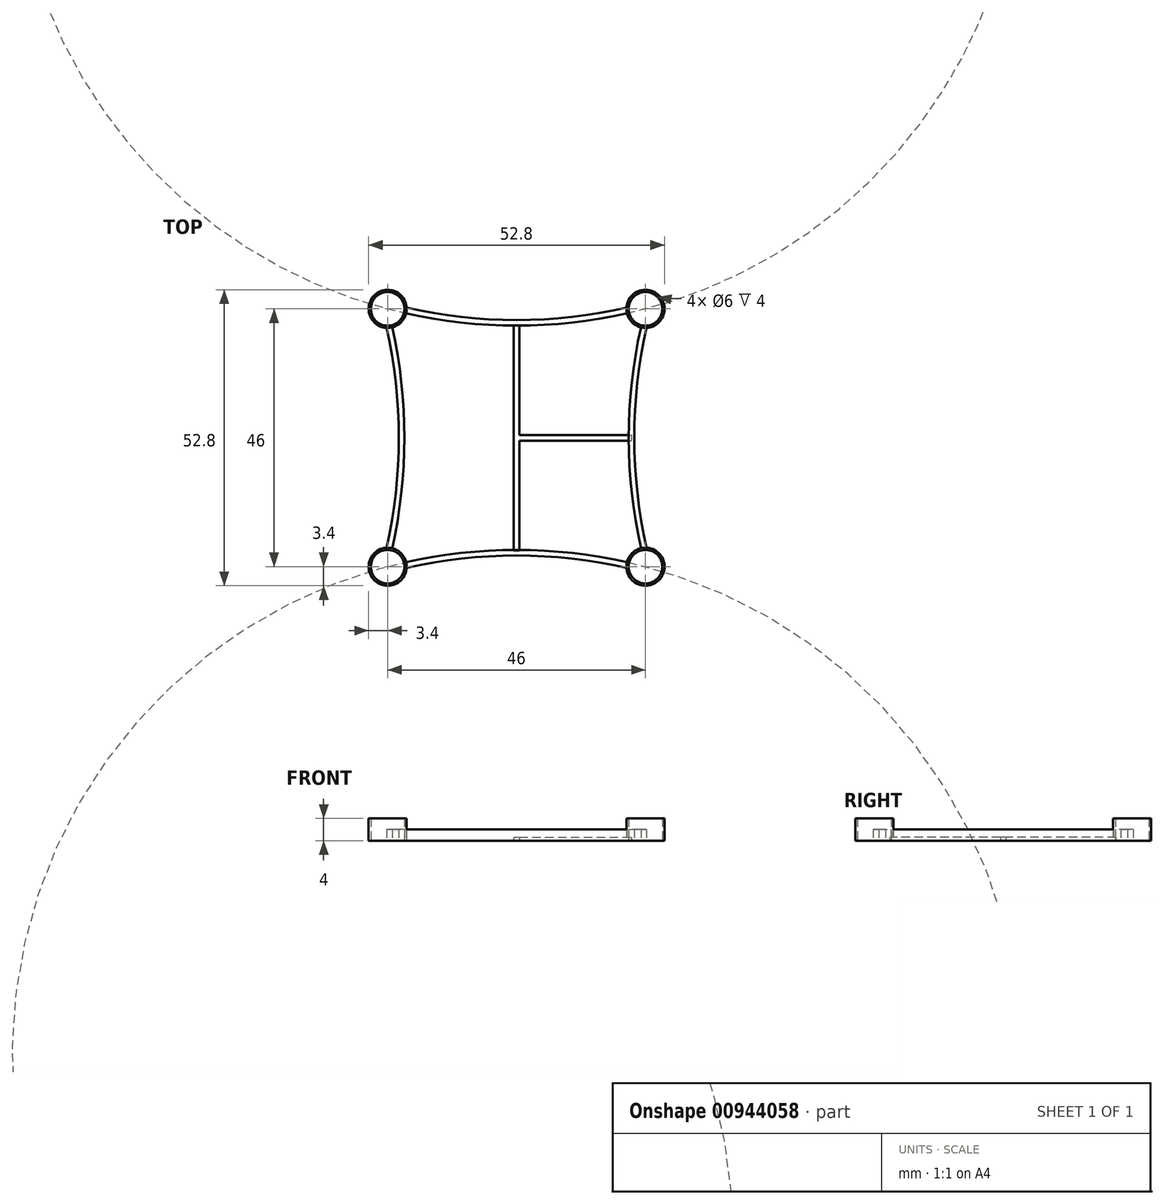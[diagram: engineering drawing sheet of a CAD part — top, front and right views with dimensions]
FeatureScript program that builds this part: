
annotation { "Feature Type Name" : "Feature", "Feature Type Description" : "" }
export const myFeature = defineFeature(function(context is Context, id is Id, definition is map)
    precondition{}
    {
        {
            var Q0;
            Q0=qCreatedBy(makeId("Top.planeOp"),FACE);
            var sketch = newSketch(context, id + "F0", { "sketchPlane" : qUnion([Q0])});
            skPoint(sketch, "E0.middle", {"position": v(0, 0) * mm});
            skArc(sketch, "E1", {"start": v(-22.2, -19.7) * mm, "mid": v(-20.01, 0) * mm, "end": v(-22.19, 19.68) * mm});
            skArc(sketch, "E2.MirrorCS", {"start": v(22.2, -19.7) * mm, "mid": v(20.01, 0) * mm, "end": v(22.2, 19.7) * mm});
            skArc(sketch, "E3", {"start": v(19.7, -22.2) * mm, "mid": v(0, -20.01) * mm, "end": v(-19.7, -22.2) * mm});
            skArc(sketch, "E4.MirrorCS", {"start": v(19.7, 22.2) * mm, "mid": v(0, 20.01) * mm, "end": v(-19.7, 22.2) * mm});
            skPoint(sketch, "E5.orphan", {"position": v(-23, 23) * mm});
            skPoint(sketch, "E6.orphan", {"position": v(23, -23) * mm});
            skPoint(sketch, "E7.orphan", {"position": v(23, 23) * mm});
            skArc(sketch, "E8.0", {"start": v(19.6, 23.2) * mm, "mid": v(0, 21) * mm, "end": v(-19.61, 23.19) * mm});
            skArc(sketch, "E9.1.0", {"start": v(-23.2, 19.6) * mm, "mid": v(-21, 0) * mm, "end": v(-23.19, -19.61) * mm});
            skArc(sketch, "E9.2.0", {"start": v(-19.6, -23.2) * mm, "mid": v(0, -21) * mm, "end": v(19.61, -23.19) * mm});
            skArc(sketch, "E9.3.0", {"start": v(23.2, -19.6) * mm, "mid": v(21, 0) * mm, "end": v(23.19, 19.61) * mm});
            skLineSegment(sketch, "E10", {"start": v(-23.19, -19.61) * mm, "end": v(-22.2, -19.7) * mm});
            skLineSegment(sketch, "E11", {"start": v(-19.7, -22.2) * mm, "end": v(-19.6, -23.2) * mm});
            skLineSegment(sketch, "E12", {"start": v(-19.61, 23.19) * mm, "end": v(-19.7, 22.2) * mm});
            skLineSegment(sketch, "E13", {"start": v(-22.19, 19.68) * mm, "end": v(-23.2, 19.6) * mm});
            skLineSegment(sketch, "E14", {"start": v(19.61, -23.19) * mm, "end": v(19.7, -22.2) * mm});
            skLineSegment(sketch, "E15", {"start": v(22.2, -19.7) * mm, "end": v(23.2, -19.6) * mm});
            skLineSegment(sketch, "E16", {"start": v(22.2, 19.7) * mm, "end": v(23.19, 19.61) * mm});
            skLineSegment(sketch, "E17", {"start": v(19.6, 23.2) * mm, "end": v(19.7, 22.2) * mm});
            skSolve(sketch);
        }
        {
            var Q0;
            Q0=qCreatedBy(makeId("Top.planeOp"),FACE);
            var sketch = newSketch(context, id + "F1", { "sketchPlane" : qUnion([Q0])});
            skCircle(sketch, "E18", {"center": v(-23, -23) * mm, "radius": 3.4 * mm});
            skCircle(sketch, "E19", {"center": v(-23, -23) * mm, "radius": 3 * mm});
            skCircle(sketch, "E20.1.0", {"center": v(23, -23) * mm, "radius": 3 * mm});
            skCircle(sketch, "E20.1.1", {"center": v(23, -23) * mm, "radius": 3.4 * mm});
            skCircle(sketch, "E20.2.0", {"center": v(23, 23) * mm, "radius": 3 * mm});
            skCircle(sketch, "E20.2.1", {"center": v(23, 23) * mm, "radius": 3.4 * mm});
            skCircle(sketch, "E20.3.0", {"center": v(-23, 23) * mm, "radius": 3 * mm});
            skCircle(sketch, "E20.3.1", {"center": v(-23, 23) * mm, "radius": 3.4 * mm});
            skPoint(sketch, "E20.center", {"position": v(0, 0) * mm});
            skSolve(sketch);
        }
        {
            var Q0;
            Q0 = qSketchRegion(id + "F1", true);
            extrude(context, id + "F2", {"entities" : qUnion([Q0]), "depth" : 4 * mm, "offsetDistance" : 25 * mm});
        }
        {
            var Q0;
            Q0 = qSketchRegion(id + "F0", true);
            extrude(context, id + "F3", {"entities" : qUnion([Q0]), "depth" : 2 * mm, "offsetDistance" : 25 * mm});
        }
        {
            var Q0;
            Q0=qCreatedBy(makeId("Top.planeOp"),FACE);
            var sketch = newSketch(context, id + "F4", { "sketchPlane" : qUnion([Q0])});
            skLineSegment(sketch, "E21", {"start": v(0.5, 20.12) * mm, "end": v(0.5, -20.24) * mm});
            skLineSegment(sketch, "E22", {"start": v(0, 0.5) * mm, "end": v(20.52, 0.5) * mm});
            skLineSegment(sketch, "E23.0", {"start": v(-0.5, 20.12) * mm, "end": v(-0.5, -20.24) * mm});
            skLineSegment(sketch, "E24", {"start": v(-0.5, 20.12) * mm, "end": v(0.5, 20.12) * mm});
            skLineSegment(sketch, "E25", {"start": v(-0.5, -20.24) * mm, "end": v(0.5, -20.24) * mm});
            skLineSegment(sketch, "E26.0", {"start": v(0, -0.5) * mm, "end": v(20.52, -0.5) * mm});
            skLineSegment(sketch, "E27", {"start": v(20.52, 0.5) * mm, "end": v(20.52, -0.5) * mm});
            skLineSegment(sketch, "E28", {"start": v(0, 0.5) * mm, "end": v(0, -0.5) * mm});
            skSolve(sketch);
        }
        {
            var Q0;
            Q0 = qSketchRegion(id + "F4", true);
            extrude(context, id + "F5", {"entities" : qUnion([Q0]), "depth" : .6 * mm, "offsetDistance" : 25 * mm});
        }
    });
